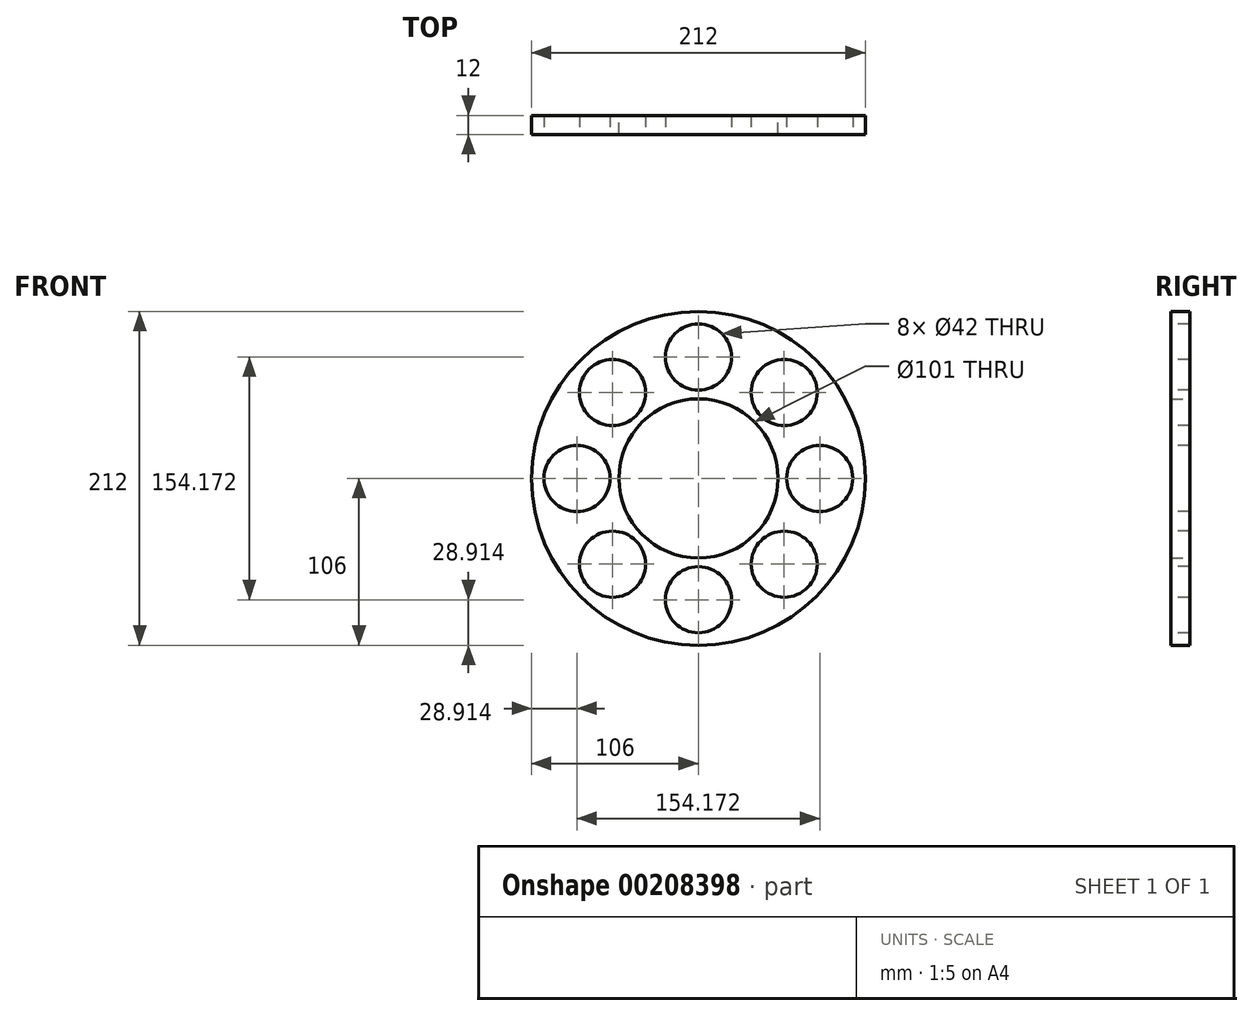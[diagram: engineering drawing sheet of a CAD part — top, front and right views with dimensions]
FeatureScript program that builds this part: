
annotation { "Feature Type Name" : "Feature", "Feature Type Description" : "" }
export const myFeature = defineFeature(function(context is Context, id is Id, definition is map)
    precondition{}
    {
        {
            var Q0;
            Q0=qCreatedBy(makeId("Front.planeOp"),FACE);
            var sketch = newSketch(context, id + "F0", { "sketchPlane" : qUnion([Q0])});
            skCircle(sketch, "E0", {"center": v(0, 0) * mm, "radius": 50.5 * mm});
            skCircle(sketch, "E1", {"center": v(0, 0) * mm, "radius": 106 * mm});
            skSolve(sketch);
        }
        {
            var Q0;
            Q0 = qSketchRegion(id + "F0", true);
            extrude(context, id + "F1", {"entities" : qUnion([Q0]), "depth" : 12 * mm, "symmetric" : true});
        }
        {
            var Q0;
            Q0=makeQuery(id+"F1.opExtrude","CAP_FACE",FACE,{"disambiguationData":[OSD([sQuery(id+"F0.wireOp",EDGE,"E0"),sQuery(id+"F0.wireOp",EDGE,"E1")])],"isStart":false});
            var sketch = newSketch(context, id + "F2", { "sketchPlane" : qUnion([Q0])});
            skCircle(sketch, "E2", {"center": v(0, 77.09) * mm, "radius": 21 * mm});
            skCircle(sketch, "E3.1.0", {"center": v(54.5, 54.5) * mm, "radius": 21 * mm});
            skCircle(sketch, "E3.2.0", {"center": v(77.09, 0) * mm, "radius": 21 * mm});
            skPoint(sketch, "E3.center", {"position": v(0, 0) * mm});
            skLineSegment(sketch, "E3.anchor1", {"start": v(0, 0) * mm, "end": v(0, 77.09) * mm, "construction": true});
            skLineSegment(sketch, "E3.anchor2", {"start": v(0, 0) * mm, "end": v(77.09, 0) * mm, "construction": true});
            skCircle(sketch, "E4.1.0", {"center": v(54.5, -54.5) * mm, "radius": 21 * mm});
            skCircle(sketch, "E4.2.0", {"center": v(0, -77.09) * mm, "radius": 21 * mm});
            skLineSegment(sketch, "E4.anchor2", {"start": v(0, 0) * mm, "end": v(0, -77.09) * mm, "construction": true});
            skCircle(sketch, "E5.1.0", {"center": v(-54.5, -54.5) * mm, "radius": 21 * mm});
            skCircle(sketch, "E5.2.0", {"center": v(-77.09, 0) * mm, "radius": 21 * mm});
            skLineSegment(sketch, "E5.anchor2", {"start": v(0, 0) * mm, "end": v(-77.09, 0) * mm, "construction": true});
            skCircle(sketch, "E6.1.0", {"center": v(-54.5, 54.5) * mm, "radius": 21 * mm});
            skSolve(sketch);
        }
        {
            var Q0;
            Q0 = qSketchRegion(id + "F2", true);
            extrude(context, id + "F3", {"entities" : qUnion([Q0]), "operationType" : NewBodyOperationType.ADD, "depth" : 12 * mm});
        }
        {
            var Q0;
            Q0=makeQuery(id+"F3.opExtrude","CAP_FACE",FACE,{"disambiguationData":[OSD([sQuery(id+"F2.wireOp",EDGE,"E5.2.0")])],"isStart":false});
            var Q1;
            Q1=makeQuery(id+"F3.opExtrude","CAP_FACE",FACE,{"disambiguationData":[OSD([sQuery(id+"F2.wireOp",EDGE,"E6.1.0")])],"isStart":false});
            var Q2;
            Q2=makeQuery(id+"F3.opExtrude","CAP_FACE",FACE,{"disambiguationData":[OSD([sQuery(id+"F2.wireOp",EDGE,"E3.2.0")])],"isStart":false});
            var Q3;
            Q3=makeQuery(id+"F3.opExtrude","CAP_FACE",FACE,{"disambiguationData":[OSD([sQuery(id+"F2.wireOp",EDGE,"E4.1.0")])],"isStart":false});
            var Q4;
            Q4=makeQuery(id+"F3.opExtrude","CAP_FACE",FACE,{"disambiguationData":[OSD([sQuery(id+"F2.wireOp",EDGE,"E4.2.0")])],"isStart":false});
            var Q5;
            Q5=makeQuery(id+"F3.opExtrude","CAP_FACE",FACE,{"disambiguationData":[OSD([sQuery(id+"F2.wireOp",EDGE,"E5.1.0")])],"isStart":false});
            var Q6;
            Q6=makeQuery(id+"F3.opExtrude","CAP_FACE",FACE,{"disambiguationData":[OSD([sQuery(id+"F2.wireOp",EDGE,"E2")])],"isStart":false});
            var Q7;
            Q7=makeQuery(id+"F3.opExtrude","CAP_FACE",FACE,{"disambiguationData":[OSD([sQuery(id+"F2.wireOp",EDGE,"E3.1.0")])],"isStart":false});
            extrude(context, id + "F4", {"entities" : qUnion([Q0, Q1, Q2, Q3, Q4, Q5, Q6, Q7]), "operationType" : NewBodyOperationType.REMOVE, "oppositeDirection" : true, "depth" : 50 * mm, "symmetric" : true});
        }
    });
